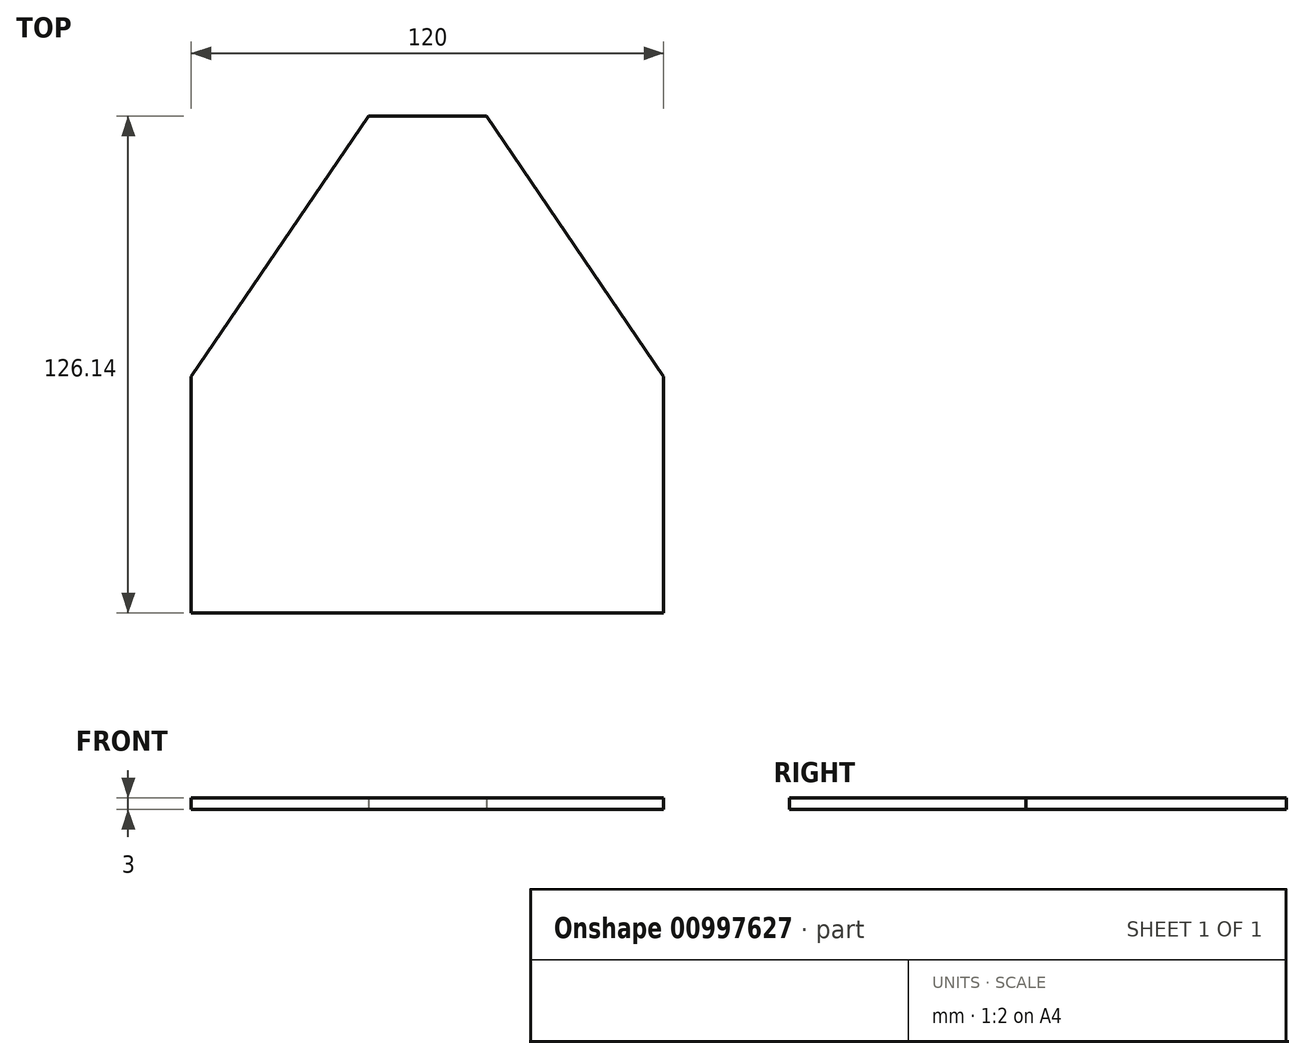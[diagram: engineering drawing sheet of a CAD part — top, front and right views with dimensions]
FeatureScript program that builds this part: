
annotation { "Feature Type Name" : "Feature", "Feature Type Description" : "" }
export const myFeature = defineFeature(function(context is Context, id is Id, definition is map)
    precondition{}
    {
        {
            var Q0;
            Q0=qCreatedBy(makeId("Top.planeOp"),FACE);
            var sketch = newSketch(context, id + "F0", { "sketchPlane" : qUnion([Q0])});
            skLineSegment(sketch, "E0", {"start": v(-61.24, -60) * mm, "end": v(58.76, -60) * mm});
            skLineSegment(sketch, "E1", {"start": v(58.76, -60) * mm, "end": v(58.76, 0) * mm});
            skLineSegment(sketch, "E2", {"start": v(58.76, 0) * mm, "end": v(13.76, 66.14) * mm});
            skLineSegment(sketch, "E3", {"start": v(13.76, 66.14) * mm, "end": v(-16.24, 66.14) * mm});
            skLineSegment(sketch, "E4", {"start": v(-61.24, 0) * mm, "end": v(-61.24, -60) * mm});
            skLineSegment(sketch, "E5", {"start": v(-61.24, 0) * mm, "end": v(-16.24, 66.14) * mm});
            skSolve(sketch);
        }
        {
            var Q0;
            Q0=makeQuery(id+"F0.imprint","IMPRINT",FACE,{"disambiguationData":[TD([[makeQuery(id+"F0.imprint","IMPRINT",EDGE,{"derivedFrom":sQuery(id+"F0.wireOp",EDGE,"E0")}),1.0]])]});
            extrude(context, id + "F1", {"entities" : qUnion([Q0]), "depth" : 3 * mm, "offsetDistance" : 25 * mm});
        }
    });
